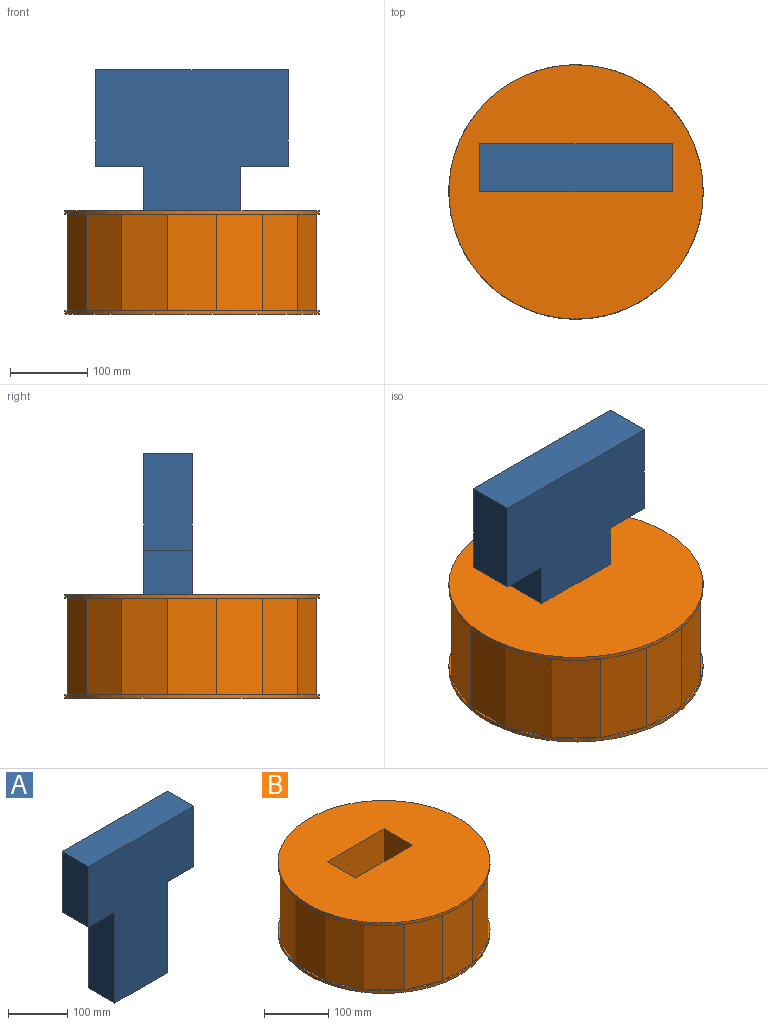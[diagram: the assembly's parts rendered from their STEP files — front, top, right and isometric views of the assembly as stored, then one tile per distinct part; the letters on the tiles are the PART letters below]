
ASSEMBLY  parts=2 mates=1
PART A: 10 faces, bbox 250x62.5x312.5 mm
  f0: plane 187.5x62.5mm, normal (1,0,0), area 11718.7mm2, adj f1,f7,f8,f9
  f1: plane 62.5x62.5mm, normal (0,0,-1), area 3906.2mm2, adj f0,f2,f8,f9
  f2: plane 125x62.5mm, normal (1,0,0), area 7812.5mm2, adj f1,f3,f8,f9
  f3: plane 250x62.5mm, normal (0,0,1), area 15625mm2, adj f2,f4,f8,f9
  f4: plane 125x62.5mm, normal (-1,0,0), area 7812.5mm2, adj f3,f5,f8,f9
  f5: plane 62.5x62.5mm, normal (0,0,-1), area 3906.2mm2, adj f4,f6,f8,f9
  f6: plane 187.5x62.5mm, normal (-1,0,0), area 11718.8mm2, adj f5,f7,f8,f9
  f7: plane 125x62.5mm, normal (0,0,-1), area 7812.5mm2, adj f0,f6,f8,f9
  f8: plane 312.5x250mm, normal (0,-1,0), area 54687.5mm2, adj f0,f1,f2,f3,f4,f5,f6,f7
  f9: plane 312.5x250mm, normal (0,1,0), area 54687.5mm2, adj f0,f1,f2,f3,f4,f5,f6,f7
PART B: 57 faces, bbox 330.1x330.1x134.5 mm
  f0: plane 330.08x330.08mm, normal (0,0,1), area 77756.8mm2, adj f51,f52,f53,f54,f55
  f1: plane 59.49x24.64mm, normal (0,0,1), area 136.4mm2, adj f17,f19
  f2: plane 64.39x3.17mm, normal (0,0,1), area 136.4mm2, adj f17,f34
  f3: plane 59.49x24.64mm, normal (0,0,1), area 136.4mm2, adj f17,f33
  f4: plane 45.53x45.53mm, normal (0,0,1), area 136.4mm2, adj f17,f32
  f5: plane 59.49x24.64mm, normal (0,0,1), area 136.4mm2, adj f17,f31
  f6: plane 64.39x3.17mm, normal (0,0,1), area 136.4mm2, adj f17,f30
  f7: plane 59.49x24.64mm, normal (0,0,1), area 136.4mm2, adj f17,f29
  f8: plane 45.53x45.53mm, normal (0,0,1), area 136.4mm2, adj f17,f28
  f9: plane 59.49x24.64mm, normal (0,0,1), area 136.4mm2, adj f17,f27
  f10: plane 64.39x3.17mm, normal (0,0,1), area 136.4mm2, adj f17,f26
  f11: plane 59.49x24.64mm, normal (0,0,1), area 136.4mm2, adj f17,f25
  f12: plane 45.53x45.53mm, normal (0,0,1), area 136.4mm2, adj f17,f24
  f13: plane 59.49x24.64mm, normal (0,0,1), area 136.4mm2, adj f17,f23
  f14: plane 64.39x3.17mm, normal (0,0,1), area 136.4mm2, adj f17,f22
  f15: plane 59.49x24.64mm, normal (0,0,1), area 136.4mm2, adj f17,f21
  f16: plane 45.53x45.53mm, normal (0,0,1), area 136.4mm2, adj f17,f20
  f17: cylinder r=165.04mm len=330.08mm, axis (0,0,1), area 4938.5mm2, adj f1,f2,f3,f4,f5,f6,f7,f8
  f18: plane 330.08x330.08mm, normal (0,0,-1), area 85569.3mm2, adj f17
  f19: plane 125x59.49mm, normal (-0.38,0.92,0), area 8049.3mm2, adj f1,f20,f34,f35
  f20: plane 125x45.53mm, normal (-0.71,0.71,0), area 8049.3mm2, adj f16,f19,f21,f36
  f21: plane 125x59.49mm, normal (-0.92,0.38,0), area 8049.3mm2, adj f15,f20,f22,f37
  f22: plane 125x64.39mm, normal (-1,0,0), area 8049.3mm2, adj f14,f21,f23,f38
  f23: plane 125x59.49mm, normal (-0.92,-0.38,0), area 8049.3mm2, adj f13,f22,f24,f39
  f24: plane 125x45.53mm, normal (-0.71,-0.71,0), area 8049.3mm2, adj f12,f23,f25,f40
  f25: plane 125x59.49mm, normal (-0.38,-0.92,0), area 8049.3mm2, adj f11,f24,f26,f41
  f26: plane 125x64.39mm, normal (0,-1,0), area 8049.3mm2, adj f10,f25,f27,f42
  f27: plane 125x59.49mm, normal (0.38,-0.92,0), area 8049.3mm2, adj f9,f26,f28,f43
  f28: plane 125x45.53mm, normal (0.71,-0.71,0), area 8049.3mm2, adj f8,f27,f29,f44
  f29: plane 125x59.49mm, normal (0.92,-0.38,0), area 8049.3mm2, adj f7,f28,f30,f45
  f30: plane 125x64.39mm, normal (1,0,0), area 8049.3mm2, adj f6,f29,f31,f46
  f31: plane 125x59.49mm, normal (0.92,0.38,0), area 8049.3mm2, adj f5,f30,f32,f47
  f32: plane 125x45.53mm, normal (0.71,0.71,0), area 8049.3mm2, adj f4,f31,f33,f48
  f33: plane 125x59.49mm, normal (0.38,0.92,0), area 8049.3mm2, adj f3,f32,f34,f49
  f34: plane 125x64.39mm, normal (0,1,0), area 8049.3mm2, adj f2,f19,f33,f50
  f35: plane 59.49x24.64mm, normal (0,0,-1), area 136.4mm2, adj f19,f51
  f36: plane 45.53x45.53mm, normal (0,0,-1), area 136.4mm2, adj f20,f51
  f37: plane 59.49x24.64mm, normal (0,0,-1), area 136.4mm2, adj f21,f51
  f38: plane 64.39x3.17mm, normal (0,0,-1), area 136.4mm2, adj f22,f51
  f39: plane 59.49x24.64mm, normal (0,0,-1), area 136.4mm2, adj f23,f51
  f40: plane 45.53x45.53mm, normal (0,0,-1), area 136.4mm2, adj f24,f51
  f41: plane 59.49x24.64mm, normal (0,0,-1), area 136.4mm2, adj f25,f51
  f42: plane 64.39x3.17mm, normal (0,0,-1), area 136.4mm2, adj f26,f51
  f43: plane 59.49x24.64mm, normal (0,0,-1), area 136.4mm2, adj f27,f51
  f44: plane 45.53x45.53mm, normal (0,0,-1), area 136.4mm2, adj f28,f51
  f45: plane 59.49x24.64mm, normal (0,0,-1), area 136.4mm2, adj f29,f51
  f46: plane 64.39x3.17mm, normal (0,0,-1), area 136.4mm2, adj f30,f51
  f47: plane 59.49x24.64mm, normal (0,0,-1), area 136.4mm2, adj f31,f51
  f48: plane 45.53x45.53mm, normal (0,0,-1), area 136.4mm2, adj f32,f51
  f49: plane 59.49x24.64mm, normal (0,0,-1), area 136.4mm2, adj f33,f51
  f50: plane 64.39x3.17mm, normal (0,0,-1), area 136.4mm2, adj f34,f51
  f51: cylinder r=165.04mm len=330.08mm, axis (0,0,-1), area 4938.5mm2, adj f0,f35,f36,f37,f38,f39,f40,f41
  f52: plane 129.76x62.5mm, normal (-1,0,0), area 8110.2mm2, adj f0,f53,f55,f56
  f53: plane 129.76x125mm, normal (0,-1,0), area 16220.3mm2, adj f0,f52,f54,f56
  f54: plane 129.76x62.5mm, normal (1,0,0), area 8110.2mm2, adj f0,f53,f55,f56
  f55: plane 129.76x125mm, normal (0,1,0), area 16220.3mm2, adj f0,f52,f54,f56
  f56: plane 125x62.5mm, normal (0,0,1), area 7812.5mm2, adj f52,f53,f54,f55
PLACE A at identity
PLACE B at identity fixed
MATE slider A.f7 <-> B.f56  axis (0,0,-1) through (0,31.25,0)mm
